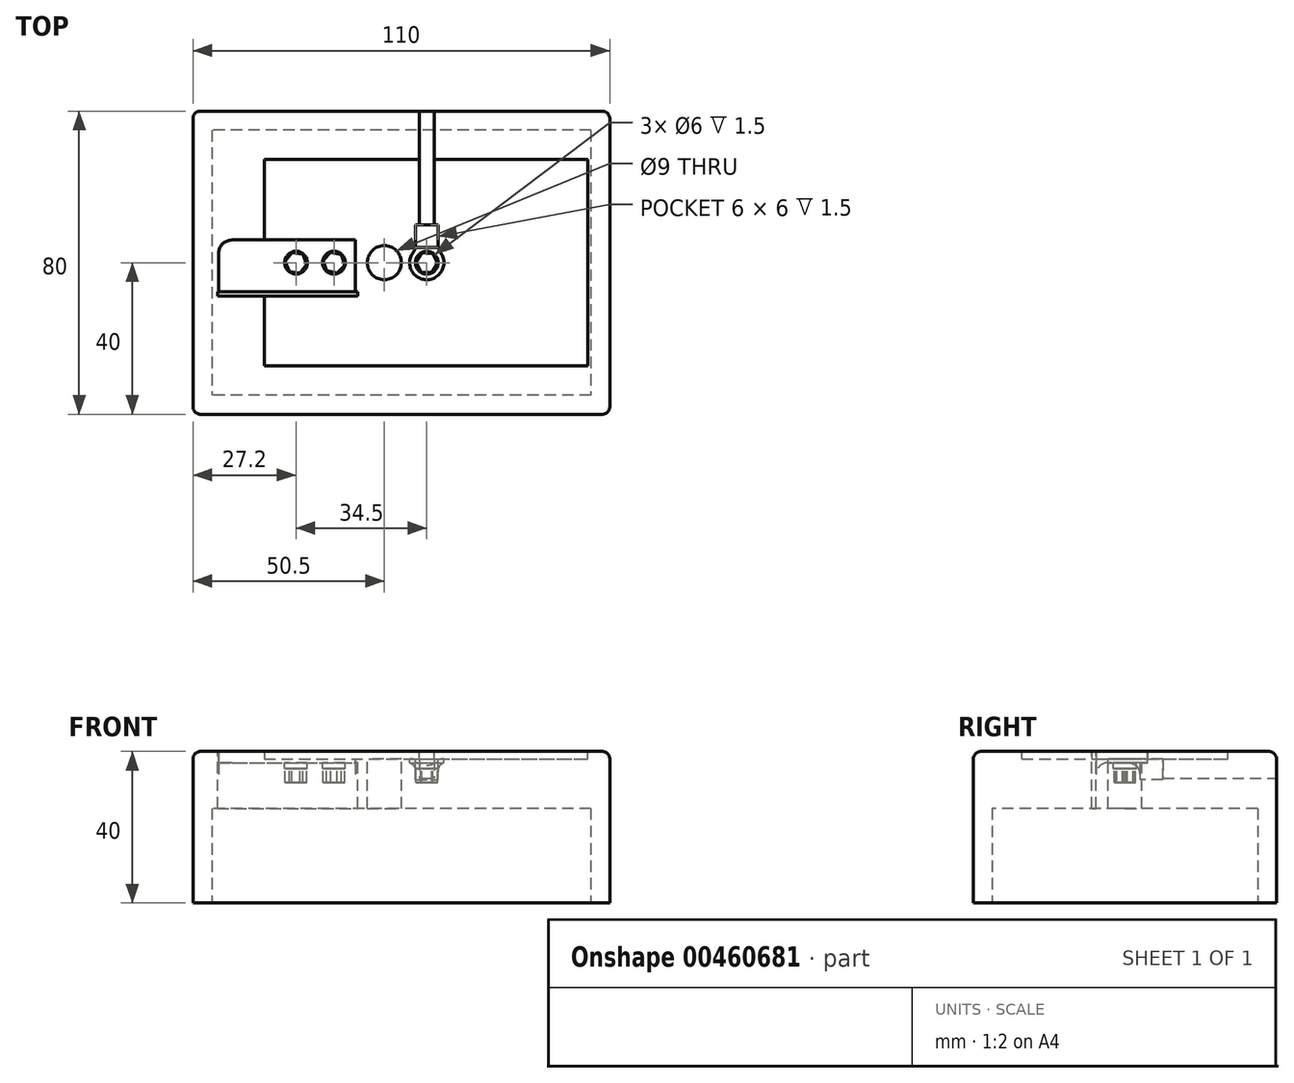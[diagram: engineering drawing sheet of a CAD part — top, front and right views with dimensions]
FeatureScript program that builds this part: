
annotation { "Feature Type Name" : "Feature", "Feature Type Description" : "" }
export const myFeature = defineFeature(function(context is Context, id is Id, definition is map)
    precondition{}
    {
        {
            var Q0;
            Q0=qCreatedBy(makeId("Top.planeOp"),FACE);
            var sketch = newSketch(context, id + "F0", { "sketchPlane" : qUnion([Q0])});
            skLineSegment(sketch, "E0.bottom", {"start": v(-55, -40) * mm, "end": v(55, -40) * mm});
            skLineSegment(sketch, "E0.top", {"start": v(-55, 40) * mm, "end": v(55, 40) * mm});
            skLineSegment(sketch, "E0.left", {"start": v(-55, -40) * mm, "end": v(-55, 40) * mm});
            skLineSegment(sketch, "E0.right", {"start": v(55, -40) * mm, "end": v(55, 40) * mm});
            skSolve(sketch);
        }
        {
            var Q0;
            Q0=makeQuery(id+"F0.imprint","IMPRINT",FACE,{"disambiguationData":[TD([[makeQuery(id+"F0.imprint","IMPRINT",EDGE,{"derivedFrom":sQuery(id+"F0.wireOp",EDGE,"E0.bottom")}),1.0]])]});
            extrude(context, id + "F1", {"entities" : qUnion([Q0]), "oppositeDirection" : true, "depth" : 40 * mm, "offsetDistance" : 25 * mm});
        }
        {
            var Q0;
            Q0=makeQuery(id+"F1.opExtrude","CAP_EDGE",EDGE,{"disambiguationData":[OSD([sQuery(id+"F0.wireOp",EDGE,"E0.top")])],"isStart":true});
            var Q1;
            Q1=makeQuery(id+"F1.opExtrude","CAP_EDGE",EDGE,{"disambiguationData":[OSD([sQuery(id+"F0.wireOp",EDGE,"E0.right")])],"isStart":true});
            var Q2;
            Q2=makeQuery(id+"F1.opExtrude","CAP_EDGE",EDGE,{"disambiguationData":[OSD([sQuery(id+"F0.wireOp",EDGE,"E0.bottom")])],"isStart":true});
            var Q3;
            Q3=makeQuery(id+"F1.opExtrude","CAP_EDGE",EDGE,{"disambiguationData":[OSD([sQuery(id+"F0.wireOp",EDGE,"E0.left")])],"isStart":true});
            var Q4;
            Q4=makeQuery(id+"F1.opExtrude","SWEPT_EDGE",EDGE,{"disambiguationData":[OSD([sQuery(id+"F0.wireOp",EDGE,"E0.top"),sQuery(id+"F0.wireOp",EDGE,"E0.right")])]});
            var Q5;
            Q5=makeQuery(id+"F1.opExtrude","SWEPT_EDGE",EDGE,{"disambiguationData":[OSD([sQuery(id+"F0.wireOp",EDGE,"E0.bottom"),sQuery(id+"F0.wireOp",EDGE,"E0.right")])]});
            var Q6;
            Q6=makeQuery(id+"F1.opExtrude","SWEPT_EDGE",EDGE,{"disambiguationData":[OSD([sQuery(id+"F0.wireOp",EDGE,"E0.top"),sQuery(id+"F0.wireOp",EDGE,"E0.left")])]});
            var Q7;
            Q7=makeQuery(id+"F1.opExtrude","SWEPT_EDGE",EDGE,{"disambiguationData":[OSD([sQuery(id+"F0.wireOp",EDGE,"E0.bottom"),sQuery(id+"F0.wireOp",EDGE,"E0.left")])]});
            fillet(context, id + "F2", {"entities" : qUnion([Q0, Q1, Q2, Q3, Q4, Q5, Q6, Q7]), "tangentPropagation" : true, "radius" : 2 * mm, "defaultsChanged" : false, "vertexSettings" : [], "allowEdgeOverflow" : false});
        }
        {
            var Q0;
            Q0=qCreatedBy(makeId("Top.planeOp"),FACE);
            var sketch = newSketch(context, id + "F3", { "sketchPlane" : qUnion([Q0])});
            skLineSegment(sketch, "E1.bottom", {"start": v(-36.2, -27.2) * mm, "end": v(49.2, -27.2) * mm});
            skLineSegment(sketch, "E1.top", {"start": v(-36.2, 27.2) * mm, "end": v(49.2, 27.2) * mm});
            skLineSegment(sketch, "E1.left", {"start": v(-36.2, -27.2) * mm, "end": v(-36.2, 27.2) * mm});
            skLineSegment(sketch, "E1.right", {"start": v(49.2, -27.2) * mm, "end": v(49.2, 27.2) * mm});
            skSolve(sketch);
        }
        {
            var Q0;
            Q0 = qSketchRegion(id + "F3", true);
            extrude(context, id + "F4", {"entities" : qUnion([Q0]), "operationType" : NewBodyOperationType.REMOVE, "oppositeDirection" : true, "depth" : 2 * mm, "offsetDistance" : 25 * mm});
        }
        {
            var Q0;
            Q0=qCreatedBy(makeId("Top.planeOp"),FACE);
            var sketch = newSketch(context, id + "F5", { "sketchPlane" : qUnion([Q0])});
            skCircle(sketch, "E2.cCircle", {"center": v(6.7, 0) * mm, "radius": 2.88 * mm, "construction": true});
            skLineSegment(sketch, "E2.0", {"start": v(8.26, 2.41) * mm, "end": v(9.57, -0.15) * mm});
            skLineSegment(sketch, "E2.1", {"start": v(9.57, -0.15) * mm, "end": v(8, -2.56) * mm});
            skLineSegment(sketch, "E2.2", {"start": v(8, -2.56) * mm, "end": v(5.14, -2.41) * mm});
            skLineSegment(sketch, "E2.3", {"start": v(5.14, -2.41) * mm, "end": v(3.83, 0.15) * mm});
            skLineSegment(sketch, "E2.4", {"start": v(3.83, 0.15) * mm, "end": v(5.4, 2.56) * mm});
            skLineSegment(sketch, "E2.5", {"start": v(5.4, 2.56) * mm, "end": v(8.26, 2.41) * mm});
            skCircle(sketch, "E3.cCircle", {"center": v(-17.8, 0) * mm, "radius": 2.88 * mm, "construction": true});
            skLineSegment(sketch, "E3.0", {"start": v(-15.86, 2.12) * mm, "end": v(-15, -0.62) * mm});
            skLineSegment(sketch, "E3.1", {"start": v(-15, -0.62) * mm, "end": v(-16.93, -2.74) * mm});
            skLineSegment(sketch, "E3.2", {"start": v(-16.93, -2.74) * mm, "end": v(-19.74, -2.12) * mm});
            skLineSegment(sketch, "E3.3", {"start": v(-19.74, -2.12) * mm, "end": v(-20.6, 0.62) * mm});
            skLineSegment(sketch, "E3.4", {"start": v(-20.6, 0.62) * mm, "end": v(-18.67, 2.74) * mm});
            skLineSegment(sketch, "E3.5", {"start": v(-18.67, 2.74) * mm, "end": v(-15.86, 2.12) * mm});
            skCircle(sketch, "E4.cCircle", {"center": v(-27.8, 0) * mm, "radius": 2.88 * mm, "construction": true});
            skLineSegment(sketch, "E4.0", {"start": v(-26.04, 2.27) * mm, "end": v(-24.95, -0.4) * mm});
            skLineSegment(sketch, "E4.1", {"start": v(-24.95, -0.4) * mm, "end": v(-26.71, -2.66) * mm});
            skLineSegment(sketch, "E4.2", {"start": v(-26.71, -2.66) * mm, "end": v(-29.56, -2.27) * mm});
            skLineSegment(sketch, "E4.3", {"start": v(-29.56, -2.27) * mm, "end": v(-30.65, 0.4) * mm});
            skLineSegment(sketch, "E4.4", {"start": v(-30.65, 0.4) * mm, "end": v(-28.89, 2.66) * mm});
            skLineSegment(sketch, "E4.5", {"start": v(-28.89, 2.66) * mm, "end": v(-26.04, 2.27) * mm});
            skSolve(sketch);
        }
        {
            var Q0;
            Q0 = qSketchRegion(id + "F5", true);
            extrude(context, id + "F6", {"entities" : qUnion([Q0]), "operationType" : NewBodyOperationType.REMOVE, "oppositeDirection" : true, "depth" : 8.2 * mm, "offsetDistance" : 25 * mm});
        }
        {
            var Q0;
            Q0=qCreatedBy(makeId("Top.planeOp"),FACE);
            var sketch = newSketch(context, id + "F7", { "sketchPlane" : qUnion([Q0])});
            skCircle(sketch, "E5", {"center": v(6.7, 0) * mm, "radius": 3 * mm});
            skCircle(sketch, "E6", {"center": v(-17.8, 0) * mm, "radius": 3 * mm});
            skCircle(sketch, "E7", {"center": v(-27.8, 0) * mm, "radius": 3 * mm});
            skSolve(sketch);
        }
        {
            var Q0;
            Q0 = qSketchRegion(id + "F7", true);
            extrude(context, id + "F8", {"entities" : qUnion([Q0]), "operationType" : NewBodyOperationType.REMOVE, "oppositeDirection" : true, "depth" : 4.5 * mm, "offsetDistance" : 25 * mm});
        }
        {
            var Q0;
            Q0=qCreatedBy(makeId("Top.planeOp"),FACE);
            var sketch = newSketch(context, id + "F9", { "sketchPlane" : qUnion([Q0])});
            skLineSegment(sketch, "E8", {"start": v(-28.2, 10.25) * mm, "end": v(-28.2, -11.34) * mm, "construction": true});
            skLineSegment(sketch, "E9.bottom", {"start": v(-48.2, -8.7) * mm, "end": v(-12.2, -8.7) * mm});
            skLineSegment(sketch, "E9.top", {"start": v(-48.2, 6) * mm, "end": v(-12.2, 6) * mm});
            skLineSegment(sketch, "E9.left", {"start": v(-48.2, -8.7) * mm, "end": v(-48.2, 6) * mm});
            skLineSegment(sketch, "E9.right", {"start": v(-12.2, -8.7) * mm, "end": v(-12.2, 6) * mm});
            skSolve(sketch);
        }
        {
            var Q0;
            Q0 = qSketchRegion(id + "F9", true);
            extrude(context, id + "F10", {"entities" : qUnion([Q0]), "operationType" : NewBodyOperationType.REMOVE, "oppositeDirection" : true, "depth" : 3 * mm, "offsetDistance" : 25 * mm});
        }
        {
            var Q0;
            Q0=qCreatedBy(makeId("Top.planeOp"),FACE);
            var sketch = newSketch(context, id + "F11", { "sketchPlane" : qUnion([Q0])});
            skLineSegment(sketch, "E10.bottom", {"start": v(-48.5, -8.8) * mm, "end": v(-11.5, -8.8) * mm});
            skLineSegment(sketch, "E10.top", {"start": v(-48.5, -7.6) * mm, "end": v(-11.5, -7.6) * mm});
            skLineSegment(sketch, "E10.left", {"start": v(-48.5, -8.8) * mm, "end": v(-48.5, -7.6) * mm});
            skLineSegment(sketch, "E10.right", {"start": v(-11.5, -8.8) * mm, "end": v(-11.5, -7.6) * mm});
            skSolve(sketch);
        }
        {
            var Q0;
            Q0 = qSketchRegion(id + "F11", true);
            extrude(context, id + "F12", {"entities" : qUnion([Q0]), "operationType" : NewBodyOperationType.REMOVE, "oppositeDirection" : true, "depth" : 33 * mm, "offsetDistance" : 25 * mm});
        }
        {
            var Q0;
            Q0=qCreatedBy(makeId("Top.planeOp"),FACE);
            var sketch = newSketch(context, id + "F13", { "sketchPlane" : qUnion([Q0])});
            skCircle(sketch, "E11", {"center": v(-4.5, 0) * mm, "radius": 4.5 * mm});
            skSolve(sketch);
        }
        {
            var Q0;
            Q0 = qSketchRegion(id + "F13", true);
            extrude(context, id + "F14", {"entities" : qUnion([Q0]), "operationType" : NewBodyOperationType.REMOVE, "oppositeDirection" : true, "depth" : 50 * mm, "offsetDistance" : 25 * mm});
        }
        {
            var Q0;
            Q0=makeQuery(id+"F10.boolean.opBoolean","COPY",EDGE,{"derivedFrom":makeQuery(id+"F10.opExtrude","SWEPT_EDGE",EDGE,{"disambiguationData":[OSD([sQuery(id+"F9.wireOp",EDGE,"E9.top"),sQuery(id+"F9.wireOp",EDGE,"E9.left")])]})});
            fillet(context, id + "F15", {"entities" : qUnion([Q0]), "tangentPropagation" : true, "radius" : 3.5 * mm, "defaultsChanged" : true, "vertexSettings" : [], "allowEdgeOverflow" : false});
        }
        {
            var Q0;
            Q0=qCreatedBy(makeId("Top.planeOp"),FACE);
            var sketch = newSketch(context, id + "F16", { "sketchPlane" : qUnion([Q0])});
            skLineSegment(sketch, "E12.bottom", {"start": v(4.7, 7) * mm, "end": v(8.7, 7) * mm});
            skLineSegment(sketch, "E12.top", {"start": v(4.7, 47) * mm, "end": v(8.7, 47) * mm});
            skLineSegment(sketch, "E12.left", {"start": v(4.7, 7) * mm, "end": v(4.7, 47) * mm});
            skLineSegment(sketch, "E12.right", {"start": v(8.7, 7) * mm, "end": v(8.7, 47) * mm});
            skSolve(sketch);
        }
        {
            var Q0;
            Q0 = qSketchRegion(id + "F16", true);
            extrude(context, id + "F17", {"entities" : qUnion([Q0]), "operationType" : NewBodyOperationType.REMOVE, "oppositeDirection" : true, "depth" : 7 * mm, "offsetDistance" : 25 * mm});
        }
        {
            var Q0;
            Q0 = qSketchRegion(id + "F16", true);
            extrude(context, id + "F18", {"entities" : qUnion([Q0]), "operationType" : NewBodyOperationType.REMOVE, "oppositeDirection" : true, "depth" : 3 * mm, "offsetDistance" : 25 * mm});
        }
        {
            var Q0;
            Q0=qCreatedBy(makeId("Top.planeOp"),FACE);
            var sketch = newSketch(context, id + "F19", { "sketchPlane" : qUnion([Q0])});
            skCircle(sketch, "E13", {"center": v(6.7, 0) * mm, "radius": 4.5 * mm});
            skSolve(sketch);
        }
        {
            var Q0;
            Q0 = qSketchRegion(id + "F19", true);
            extrude(context, id + "F20", {"entities" : qUnion([Q0]), "operationType" : NewBodyOperationType.REMOVE, "oppositeDirection" : true, "depth" : 3 * mm, "offsetDistance" : 25 * mm});
        }
        {
            var Q0;
            Q0=qCreatedBy(makeId("Top.planeOp"),FACE);
            var sketch = newSketch(context, id + "F21", { "sketchPlane" : qUnion([Q0])});
            skLineSegment(sketch, "E14.bottom", {"start": v(3.72, 10) * mm, "end": v(9.72, 10) * mm});
            skLineSegment(sketch, "E14.top", {"start": v(3.72, 4) * mm, "end": v(9.72, 4) * mm});
            skLineSegment(sketch, "E14.left", {"start": v(3.72, 10) * mm, "end": v(3.72, 4) * mm});
            skLineSegment(sketch, "E14.right", {"start": v(9.72, 10) * mm, "end": v(9.72, 4) * mm});
            skSolve(sketch);
        }
        {
            var Q0;
            Q0 = qSketchRegion(id + "F21", true);
            extrude(context, id + "F22", {"entities" : qUnion([Q0]), "operationType" : NewBodyOperationType.REMOVE, "oppositeDirection" : true, "depth" : 7.5 * mm, "offsetDistance" : 25 * mm});
        }
        {
            var Q0;
            Q0=makeQuery(id+"F1.opExtrude","CAP_FACE",FACE,{"disambiguationData":[OSD([sQuery(id+"F0.wireOp",EDGE,"E0.bottom"),sQuery(id+"F0.wireOp",EDGE,"E0.top"),sQuery(id+"F0.wireOp",EDGE,"E0.left"),sQuery(id+"F0.wireOp",EDGE,"E0.right")])],"isStart":false});
            var sketch = newSketch(context, id + "F23", { "sketchPlane" : qUnion([Q0])});
            skLineSegment(sketch, "E15.bottom", {"start": v(50, -35) * mm, "end": v(-50, -35) * mm});
            skLineSegment(sketch, "E15.top", {"start": v(50, 35) * mm, "end": v(-50, 35) * mm});
            skLineSegment(sketch, "E15.left", {"start": v(50, -35) * mm, "end": v(50, 35) * mm});
            skLineSegment(sketch, "E15.right", {"start": v(-50, -35) * mm, "end": v(-50, 35) * mm});
            skPoint(sketch, "E15.middle", {"position": v(0, 0) * mm});
            skSolve(sketch);
        }
        {
            var Q0;
            Q0 = qSketchRegion(id + "F23", true);
            extrude(context, id + "F24", {"entities" : qUnion([Q0]), "operationType" : NewBodyOperationType.REMOVE, "oppositeDirection" : true, "depth" : 25 * mm, "offsetDistance" : 25 * mm});
        }
        {
            var Q0;
            Q0=makeQuery(id+"F22.boolean.opBoolean","INTERSECT",EDGE,{"disambiguationData":[OD(0.0)],"derivedFrom":[makeQuery(id+"F20.boolean.opBoolean","COPY",FACE,{"derivedFrom":makeQuery(id+"F20.opExtrude","SWEPT_FACE",FACE,{"disambiguationData":[OSD([sQuery(id+"F19.wireOp",EDGE,"E13")])]})}),makeQuery(id+"F22.opExtrude","SWEPT_FACE",FACE,{"disambiguationData":[OSD([sQuery(id+"F21.wireOp",EDGE,"E14.top")])]})]});
            var Q1;
            Q1=makeQuery(id+"F22.boolean.opBoolean","INTERSECT",EDGE,{"disambiguationData":[OD(1.0)],"derivedFrom":[makeQuery(id+"F20.boolean.opBoolean","COPY",FACE,{"derivedFrom":makeQuery(id+"F20.opExtrude","SWEPT_FACE",FACE,{"disambiguationData":[OSD([sQuery(id+"F19.wireOp",EDGE,"E13")])]})}),makeQuery(id+"F22.opExtrude","SWEPT_FACE",FACE,{"disambiguationData":[OSD([sQuery(id+"F21.wireOp",EDGE,"E14.top")])]})]});
            fillet(context, id + "F25", {"entities" : qUnion([Q0, Q1]), "tangentPropagation" : true, "radius" : 5 * mm, "defaultsChanged" : false, "vertexSettings" : [], "allowEdgeOverflow" : false});
        }
        {
            var Q0;
            Q0=makeQuery(id+"F12.boolean.opBoolean","INTERSECT",EDGE,{"derivedFrom":[makeQuery(id+"F10.boolean.opBoolean","COPY",FACE,{"derivedFrom":makeQuery(id+"F10.opExtrude","CAP_FACE",FACE,{"disambiguationData":[OSD([sQuery(id+"F9.wireOp",EDGE,"E9.bottom"),sQuery(id+"F9.wireOp",EDGE,"E9.top"),sQuery(id+"F9.wireOp",EDGE,"E9.left"),sQuery(id+"F9.wireOp",EDGE,"E9.right")])],"isStart":false})}),makeQuery(id+"F12.opExtrude","SWEPT_FACE",FACE,{"disambiguationData":[OSD([sQuery(id+"F11.wireOp",EDGE,"E10.top")])]})]});
            fillet(context, id + "F26", {"entities" : qUnion([Q0]), "tangentPropagation" : true, "radius" : 3 * mm, "defaultsChanged" : true, "vertexSettings" : [], "allowEdgeOverflow" : false});
        }
        {
            var Q0;
            Q0=makeQuery(id+"F22.boolean.opBoolean","INTERSECT",EDGE,{"derivedFrom":[makeQuery(id+"F20.boolean.opBoolean","COPY",FACE,{"derivedFrom":makeQuery(id+"F20.opExtrude","CAP_FACE",FACE,{"disambiguationData":[OSD([sQuery(id+"F19.wireOp",EDGE,"E13")])],"isStart":false})}),makeQuery(id+"F22.opExtrude","SWEPT_FACE",FACE,{"disambiguationData":[OSD([sQuery(id+"F21.wireOp",EDGE,"E14.top")])]})]});
            fillet(context, id + "F27", {"entities" : qUnion([Q0]), "tangentPropagation" : true, "radius" : 3 * mm, "defaultsChanged" : true, "vertexSettings" : [], "allowEdgeOverflow" : false});
        }
    });
